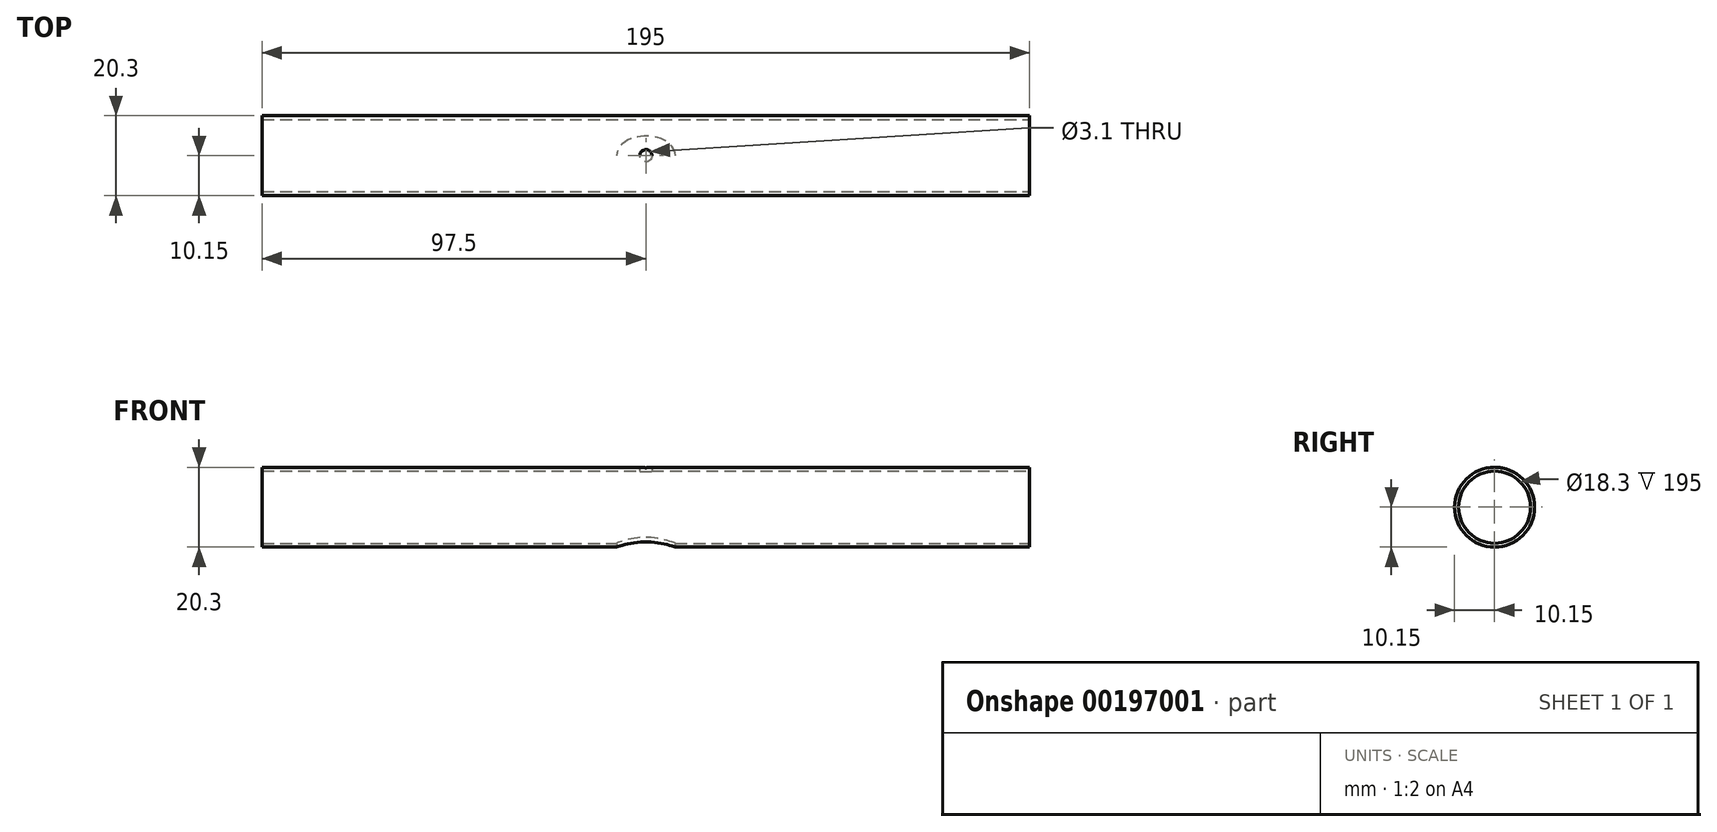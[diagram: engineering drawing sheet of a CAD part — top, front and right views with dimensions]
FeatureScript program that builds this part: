
annotation { "Feature Type Name" : "Feature", "Feature Type Description" : "" }
export const myFeature = defineFeature(function(context is Context, id is Id, definition is map)
    precondition{}
    {
        {
            var Q0;
            Q0=qCreatedBy(makeId("Right.planeOp"),FACE);
            var sketch = newSketch(context, id + "F0", { "sketchPlane" : qUnion([Q0])});
            skCircle(sketch, "E0", {"center": v(0, 0) * mm, "radius": 10.15 * mm});
            skSolve(sketch);
        }
        {
            var Q0;
            Q0 = qSketchRegion(id + "F0", true);
            extrude(context, id + "F1", {"entities" : qUnion([Q0]), "depth" : 195 * mm});
        }
        {
            var Q0;
            Q0=makeQuery(id+"F1.opExtrude","CAP_FACE",FACE,{"disambiguationData":[OSD([sQuery(id+"F0.wireOp",EDGE,"E0")])],"isStart":false});
            var sketch = newSketch(context, id + "F2", { "sketchPlane" : qUnion([Q0])});
            skCircle(sketch, "E1", {"center": v(0, 0) * mm, "radius": 9.15 * mm});
            skSolve(sketch);
        }
        {
            var Q0;
            Q0 = qSketchRegion(id + "F2", true);
            extrude(context, id + "F3", {"entities" : qUnion([Q0]), "operationType" : NewBodyOperationType.REMOVE, "endBound" : BoundingType.THROUGH_ALL, "oppositeDirection" : true, "depth" : 25 * mm});
        }
        {
            var Q0;
            Q0=qCreatedBy(makeId("Top.planeOp"),FACE);
            var sketch = newSketch(context, id + "F4", { "sketchPlane" : qUnion([Q0])});
            skLineSegment(sketch, "E2", {"start": v(0, 0) * mm, "end": v(195, 0) * mm, "construction": true});
            skEllipse(sketch, "E3", {"center": v(97.5, 0) * mm, "majorRadius": 7.5 * mm, "minorRadius": 5 * mm, "majorAxis": v(1, 0)});
            skSolve(sketch);
        }
        {
            var Q0;
            Q0 = qSketchRegion(id + "F4", true);
            extrude(context, id + "F5", {"entities" : qUnion([Q0]), "operationType" : NewBodyOperationType.REMOVE, "endBound" : BoundingType.THROUGH_ALL, "oppositeDirection" : true, "depth" : 25 * mm});
        }
        {
            var Q0;
            Q0=qCreatedBy(makeId("Top.planeOp"),FACE);
            var sketch = newSketch(context, id + "F6", { "sketchPlane" : qUnion([Q0])});
            skLineSegment(sketch, "E4", {"start": v(0, 0) * mm, "end": v(195, 0) * mm, "construction": true});
            skCircle(sketch, "E5", {"center": v(97.5, 0) * mm, "radius": 1.55 * mm});
            skSolve(sketch);
        }
        {
            var Q0;
            Q0 = qSketchRegion(id + "F6", true);
            extrude(context, id + "F7", {"entities" : qUnion([Q0]), "operationType" : NewBodyOperationType.REMOVE, "endBound" : BoundingType.THROUGH_ALL, "depth" : 25 * mm});
        }
    });
